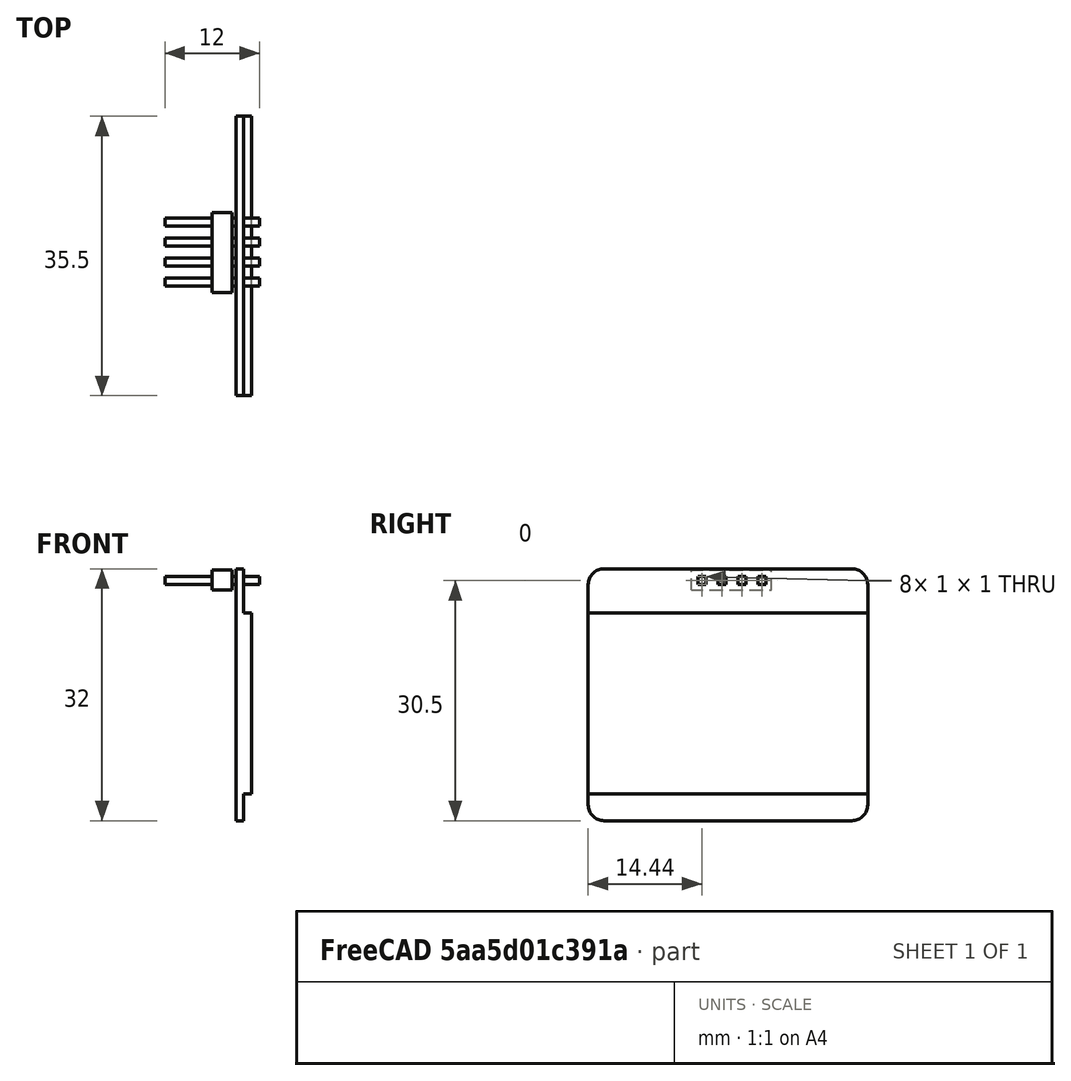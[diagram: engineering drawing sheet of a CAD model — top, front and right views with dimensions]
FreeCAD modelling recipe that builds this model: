
FCSTD DOCUMENT
Label: lcd
License: CC-BY 3.0
LicenseURL: http://creativecommons.org/licenses/by/3.0/
objects: Part::Box×10, Part::MultiFuse×6, Part::Fillet×4
note: 20 computed .brp shape members not serialized (recipe doc carries the construction recipe); baked Part::Feature solids carry a one-line shape summary decoded from their .brp

FEATURE [Part::Box] Box  label="pcb"
  Height = 32
  Length = 1
  Placement = pos=(-2,0,0) rot=(0,0,1;0rad)
  Width = 35.5
FEATURE [Part::Box] Box001  label="display"
  Height = 23
  Length = 1
  Placement = pos=(-1,0,3.4) rot=(0,0,1;0rad)
  Width = 35.5
FEATURE [Part::Box] Box002  label="Pin"
  Height = 1
  Length = 12
  Placement = pos=(-11,13.94,30) rot=(0,0,1;0rad)
  Width = 1
FEATURE [Part::Box] Box003  label="Housing"
  Height = 2.54
  Length = 2.54
  Placement = pos=(-5,13.1,29.3) rot=(0,0,1;0rad)
  Width = 2.54
FEATURE [Part::MultiFuse] Fusion  label="Pin001"
  Shapes = -> [Box002,Box003]
FEATURE [Part::Box] Box003001  label="Housing001"
  Height = 2.54
  Length = 2.54
  Placement = pos=(-5,13.1,29.3) rot=(0,0,1;0rad)
  Width = 2.54
FEATURE [Part::Box] Box002001  label="Pin002"
  Height = 1
  Length = 12
  Placement = pos=(-11,13.94,30) rot=(0,0,1;0rad)
  Width = 1
FEATURE [Part::MultiFuse] Fusion001  label="Pin003"
  Placement = pos=(0,2.54,0) rot=(0,0,1;0rad)
  Shapes = -> [Box002001,Box003001]
FEATURE [Part::Box] Box002001001  label="Pin005"
  Height = 1
  Length = 12
  Placement = pos=(-11,13.94,30) rot=(0,0,1;0rad)
  Width = 1
FEATURE [Part::Box] Box003001001  label="Housing002"
  Height = 2.54
  Length = 2.54
  Placement = pos=(-5,13.1,29.3) rot=(0,0,1;0rad)
  Width = 2.54
FEATURE [Part::MultiFuse] Fusion001001  label="Pin004"
  Placement = pos=(0,5.08,0) rot=(0,0,1;0rad)
  Shapes = -> [Box002001001,Box003001001]
FEATURE [Part::Box] Box003001001001  label="Housing003"
  Height = 2.54
  Length = 2.54
  Placement = pos=(-5,13.1,29.3) rot=(0,0,1;0rad)
  Width = 2.54
FEATURE [Part::Box] Box002001001001  label="Pin007"
  Height = 1
  Length = 12
  Placement = pos=(-11,13.94,30) rot=(0,0,1;0rad)
  Width = 1
FEATURE [Part::MultiFuse] Fusion001001001  label="Pin006"
  Placement = pos=(0,7.62,0) rot=(0,0,1;0rad)
  Shapes = -> [Box002001001001,Box003001001001]
FEATURE [Part::MultiFuse] Fusion001001002  label="Pins"
  Shapes = -> [Fusion,Fusion001,Fusion001001,Fusion001001001]
FEATURE [Part::Fillet] Fillet
  Base = -> Box
  Edges = 1 edges r=2: [Edge10]
FEATURE [Part::Fillet] Fillet001
  Base = -> Fillet
  Edges = 1 edges r=2: [Edge13]
FEATURE [Part::Fillet] Fillet002
  Base = -> Fillet001
  Edges = 1 edges r=2: [Edge17]
FEATURE [Part::Fillet] Fillet003  label="Pcb"
  Base = -> Fillet002
  Edges = 1 edges r=2: [Edge15]
FEATURE [Part::MultiFuse] Fusion001001003  label="Lcd"
  Shapes = -> [Box001,Fusion001001002,Fillet003]
